# Revit family: EDLR-E2-195-xxxx-8xx-Wx
name_source: partatom
category: Oprawy oświetleniowe
revit_build: Autodesk Revit 2017 (Build: 20190507_1515(x64)
units: mm (PartAtom-declared; Revit-internal decimal feet)

## family parameters
Numer OmniClass = 23.80.70.11
Obiekt nadrzędny = Powierzchnia
Punkt obliczania pomieszczeń = Nie
Tnij formami wycięć po wczytaniu = Tak
Typ części = Normalny
Tytuł OmniClass = Luminaries for Internal Lighting
Współdzielony = Nie
Wymiar okrągłego złącza = Użyj średnicy
Źródło światła = Tak

## types (8) — shared parameters
Emituj kształt widoczny w renderingu = Nie
Emituj ze średnicy okręgu = 180 mm  [stored 0.590551 ft]
Filtr koloru = 16777215
Kod zespołu = D5020200
Lampa = LED
Odchylenie kierunku = 90.00°
Producent = RIDI Leuchten GmbH
URL = www.ridi.de
Zmiana temperatury barwowej przyciemniania lampy = <Brak>
brand = RIDI
conformity mark = CE
electrical safety class = 1
height = 65 mm  [stored 0.213255 ft]
ingress protection (IP) code = IP20
length = 195 mm  [stored 0.639764 ft]
nominal frequency = 50-60Hz
nominal voltage = 230
voltage type (AC, DC, UC) = AC
width = 195 mm  [stored 0.639764 ft]
zero-valued in all types: Domyślna rzędna

## per-type parameters (varying)
| type | Model | Obciążenie pozorne | Plik sieci fotometrycznej | product name | rated input power | weight |
| EDLR-E2 195/1100-830 W-DALI | 0331512 | 9 VA | EDLR-E2 195_1100-840 W.IES | EDLR-E2 195/1100-830 W-DALI | 9 | 0.44kg |
| EDLR-E2 195/1100-830 W | 0321512 | 9 VA | EDLR-E2 195_1100-840 W.IES | EDLR-E2 195/1100-830 W | 9 | 0.33kg |
| EDLR-E2 195/1100-840 W | 0321511 | 9 VA | EDLR-E2 195_1100-840 W.IES | EDLR-E2 195/1100-830 W | 9 | 0.33kg |
| EDLR-E2 195/1100-840 W-DALI | 0331511 | 9 VA | EDLR-E2 195_1100-840 W.IES | EDLR-E2 195/1100-840 W-DALI | 9 | 0.443kg |
| EDLR-E2 195/2000-830 W | 0331511 | 16 VA | EDLR-E2 195_2000-840 W.IES | EDLR-E2 195/2000-830 W | 16 | 0.443kg |
| EDLR-E2 195/2000-830 W-DALI | 0331514 | 16 VA | EDLR-E2 195_2000-840 W.IES | EDLR-E2 195/2000-830 W-DALI | 16 | 0.479kg |
| EDLR-E2 195/2000-840 W | 0321513 | 16 VA | EDLR-E2 195_2000-840 W.IES | EDLR-E2 195/2000-840 W | 16 | 0.479kg |
| EDLR-E2 195/2000-840 W-DALI | 0331513 | 16 VA | EDLR-E2 195_2000-840 W.IES | EDLR-E2 195/2000-840 W-DALI | 16 | 0.479kg |

note: [stored X ft] marks values corroborated as IEEE doubles in the binary element streams (Revit-internal decimal feet)
